annotation { "Feature Type Name" : "Feature", "Feature Type Description" : "" }
export const myFeature = defineFeature(function(context is Context, id is Id, definition is map)
    precondition{}
    {
        {
            var Q0;
            Q0=qCreatedBy(makeId("Top.planeOp"),FACE);
            var sketch = newSketch(context, id + "F0", { "sketchPlane" : qUnion([Q0])});
            skArc(sketch, "E0", {"start": v(-40.95, 7.5) * mm, "mid": v(-48.45, 0) * mm, "end": v(-40.95, -7.5) * mm});
            skArc(sketch, "E1", {"start": v(-40.95, 11.5) * mm, "mid": v(-52.45, 0) * mm, "end": v(-40.95, -11.5) * mm});
            skLineSegment(sketch, "E2", {"start": v(-40.95, 7.5) * mm, "end": v(69.05, 7.5) * mm});
            skLineSegment(sketch, "E3", {"start": v(69.05, 11.5) * mm, "end": v(-40.95, 11.5) * mm});
            skLineSegment(sketch, "E4", {"start": v(-40.95, -7.5) * mm, "end": v(-26.45, -7.5) * mm});
            skLineSegment(sketch, "E5", {"start": v(69.05, -11.5) * mm, "end": v(0, -11.5) * mm});
            skArc(sketch, "E6", {"start": v(-3.98, -7.14) * mm, "mid": v(-13.37, 0.07) * mm, "end": v(-15.85, -11.5) * mm});
            skArc(sketch, "E7", {"start": v(0.66, -4.5) * mm, "mid": v(-10.95, 4.5) * mm, "end": v(-22.57, -4.5) * mm});
            skLineSegment(sketch, "E8.trimOffspring", {"start": v(-15.85, -11.5) * mm, "end": v(-40.95, -11.5) * mm});
            skLineSegment(sketch, "E9.trimOffspring", {"start": v(4.54, -7.5) * mm, "end": v(69.05, -7.5) * mm});
            skPoint(sketch, "E10.visualSharp", {"position": v(1.05, -7.5) * mm});
            skArc(sketch, "E10.filletArc", {"start": v(0.66, -4.5) * mm, "mid": v(2.09, -6.66) * mm, "end": v(4.54, -7.5) * mm});
            skPoint(sketch, "E11.visualSharp", {"position": v(-6.06, -11.5) * mm});
            skArc(sketch, "E11.filletArc", {"start": v(-3.98, -7.14) * mm, "mid": v(-2.95, -10.2) * mm, "end": v(0, -11.5) * mm});
            skPoint(sketch, "E12.visualSharp", {"position": v(-22.95, -7.5) * mm});
            skArc(sketch, "E12.filletArc", {"start": v(-26.45, -7.5) * mm, "mid": v(-24, -6.66) * mm, "end": v(-22.57, -4.5) * mm});
            skLineSegment(sketch, "E13", {"start": v(69.05, 46.2) * mm, "end": v(69.05, -31.55) * mm, "construction": true});
            skLineSegment(sketch, "E14", {"start": v(84.05, 46.35) * mm, "end": v(84.05, -33.76) * mm, "construction": true});
            skLineSegment(sketch, "E15", {"start": v(69.05, 7.5) * mm, "end": v(84.05, 6.19) * mm});
            skLineSegment(sketch, "E16", {"start": v(69.05, -7.5) * mm, "end": v(84.05, -6.19) * mm});
            skLineSegment(sketch, "E17", {"start": v(84.05, -6.19) * mm, "end": v(69.05, -11.5) * mm});
            skLineSegment(sketch, "E18", {"start": v(84.05, 6.19) * mm, "end": v(69.05, 11.5) * mm});
            skLineSegment(sketch, "E19", {"start": v(-15.85, -11.5) * mm, "end": v(0, -11.5) * mm, "construction": true});
            skLineSegment(sketch, "E20", {"start": v(-10.95, 25.74) * mm, "end": v(-10.95, -28.58) * mm, "construction": true});
            skSolve(sketch);
        }
        {
            var Q0;
            Q0=makeQuery(id+"F0.imprint","IMPRINT",FACE,{"disambiguationData":[TD([[makeQuery(id+"F0.imprint","IMPRINT",EDGE,{"derivedFrom":sQuery(id+"F0.wireOp",EDGE,"E0")}),-1.0]])]});
            var Q1;
            {var subQ5=sQuery(id+"F0.wireOp",EDGE,"zYFOjHQd-zfKD-8OcH-rvdT-M6pXXP429t8t.bottom");Q1=makeQuery(id+"F0.imprint","IMPRINT",FACE,{"disambiguationData":[TD([[makeQuery(id+"F0.imprint","IMPRINT",EDGE,{"derivedFrom":subQ5}),-1.0]])]});}
            var Q2;
            {var subQ0=sQuery(id+"F0.wireOp",EDGE,"zYFOjHQd-zfKD-8OcH-rvdT-M6pXXP429t8t.right");var subQ1=sQuery(id+"F0.wireOp",EDGE,"E2");var subQ2=makeQuery(id+"F0.imprint","INTERSECT",VERTEX,{"derivedFrom":[subQ1,subQ0]});Q2=makeQuery(id+"F0.imprint","IMPRINT",FACE,{"disambiguationData":[TD([[makeQuery(id+"F0.imprint","IMPRINT",EDGE,{"disambiguationData":[TD([[subQ2,1.0]])],"derivedFrom":subQ1}),-1.0]])]});}
            var Q3;
            {var subQ5=sQuery(id+"F0.wireOp",EDGE,"zYFOjHQd-zfKD-8OcH-rvdT-M6pXXP429t8t.top");Q3=makeQuery(id+"F0.imprint","IMPRINT",FACE,{"disambiguationData":[TD([[makeQuery(id+"F0.imprint","IMPRINT",EDGE,{"derivedFrom":subQ5}),1.0]])]});}
            extrude(context, id + "F1", {"entities" : qUnion([Q0, Q1, Q2, Q3]), "depth" : 15 * mm, "offsetDistance" : 25 * mm, "symmetric" : true});
        }
        {
            var Q0;
            Q0=qCreatedBy(makeId("Top.planeOp"),FACE);
            var sketch = newSketch(context, id + "F2", { "sketchPlane" : qUnion([Q0])});
            skArc(sketch, "E21.0.0", {"start": v(-15.85, -11.5) * mm, "mid": v(-13.37, 0.07) * mm, "end": v(-3.98, -7.14) * mm, "construction": true});
            skArc(sketch, "E21.0.1", {"start": v(-3.98, -7.14) * mm, "mid": v(-2.95, -10.2) * mm, "end": v(0, -11.5) * mm, "construction": true});
            skLineSegment(sketch, "E21.0.2", {"start": v(0, -11.5) * mm, "end": v(69.05, -11.5) * mm, "construction": true});
            skLineSegment(sketch, "E21.0.3", {"start": v(69.05, -11.5) * mm, "end": v(84.05, -6.19) * mm, "construction": true});
            skLineSegment(sketch, "E21.0.4", {"start": v(84.05, -6.19) * mm, "end": v(69.05, -7.5) * mm, "construction": true});
            skLineSegment(sketch, "E21.0.5", {"start": v(69.05, -7.5) * mm, "end": v(4.54, -7.5) * mm, "construction": true});
            skArc(sketch, "E21.0.6", {"start": v(4.54, -7.5) * mm, "mid": v(2.09, -6.66) * mm, "end": v(0.66, -4.5) * mm, "construction": true});
            skArc(sketch, "E21.0.7", {"start": v(0.66, -4.5) * mm, "mid": v(-10.95, 4.5) * mm, "end": v(-22.57, -4.5) * mm, "construction": true});
            skArc(sketch, "E21.0.8", {"start": v(-22.57, -4.5) * mm, "mid": v(-24, -6.66) * mm, "end": v(-26.45, -7.5) * mm, "construction": true});
            skLineSegment(sketch, "E21.0.9", {"start": v(-26.45, -7.5) * mm, "end": v(-40.95, -7.5) * mm, "construction": true});
            skArc(sketch, "E21.0.10", {"start": v(-40.95, -7.5) * mm, "mid": v(-48.45, 0) * mm, "end": v(-40.95, 7.5) * mm, "construction": true});
            skLineSegment(sketch, "E21.0.11", {"start": v(-40.95, 7.5) * mm, "end": v(69.05, 7.5) * mm, "construction": true});
            skLineSegment(sketch, "E21.0.12", {"start": v(69.05, 7.5) * mm, "end": v(84.05, 6.19) * mm, "construction": true});
            skLineSegment(sketch, "E21.0.13", {"start": v(84.05, 6.19) * mm, "end": v(69.05, 11.5) * mm, "construction": true});
            skLineSegment(sketch, "E21.0.14", {"start": v(69.05, 11.5) * mm, "end": v(-40.95, 11.5) * mm, "construction": true});
            skArc(sketch, "E21.0.15", {"start": v(-40.95, 11.5) * mm, "mid": v(-52.45, 0) * mm, "end": v(-40.95, -11.5) * mm, "construction": true});
            skLineSegment(sketch, "E21.0.16", {"start": v(-40.95, -11.5) * mm, "end": v(-15.85, -11.5) * mm, "construction": true});
            skCircle(sketch, "E22", {"center": v(-40.95, 0) * mm, "radius": 9 * mm});
            skCircle(sketch, "E23", {"center": v(-40.95, 0) * mm, "radius": 10 * mm});
            skLineSegment(sketch, "E24", {"start": v(-17.95, 16.7) * mm, "end": v(-17.95, -20.86) * mm, "construction": true});
            skLineSegment(sketch, "E25", {"start": v(-3.95, 17.93) * mm, "end": v(-3.95, -22.51) * mm, "construction": true});
            skArc(sketch, "E26", {"start": v(-3.95, 7.5) * mm, "mid": v(-6.58, 4.87) * mm, "end": v(-3.95, 2.25) * mm});
            skArc(sketch, "E27", {"start": v(-17.95, 2.25) * mm, "mid": v(-15.33, 4.87) * mm, "end": v(-17.95, 7.5) * mm});
            skLineSegment(sketch, "E28", {"start": v(-17.95, 2.25) * mm, "end": v(-3.95, 2.25) * mm});
            skLineSegment(sketch, "E29", {"start": v(-3.95, 7.5) * mm, "end": v(-17.95, 7.5) * mm});
            skSolve(sketch);
        }
        {
            var Q0;
            Q0=makeQuery(id+"F2.imprint","IMPRINT",FACE,{"disambiguationData":[TD([[makeQuery(id+"F2.imprint","IMPRINT",EDGE,{"derivedFrom":sQuery(id+"F2.wireOp",EDGE,"E26")}),-1.0]])]});
            extrude(context, id + "F3", {"entities" : qUnion([Q0]), "operationType" : NewBodyOperationType.ADD, "depth" : 15 * mm, "offsetDistance" : 25 * mm, "symmetric" : true});
        }
        {
            var Q0;
            Q0=makeQuery(id+"F3.boolean.opBoolean","MERGE",FACE,{"derivedFrom":[makeQuery(id+"F1.opExtrude","CAP_FACE",FACE,{"disambiguationData":[OSD([sQuery(id+"F0.wireOp",EDGE,"E0"),sQuery(id+"F0.wireOp",EDGE,"E1"),sQuery(id+"F0.wireOp",EDGE,"E2"),sQuery(id+"F0.wireOp",EDGE,"E3"),sQuery(id+"F0.wireOp",EDGE,"E4"),sQuery(id+"F0.wireOp",EDGE,"E5"),sQuery(id+"F0.wireOp",EDGE,"E6"),sQuery(id+"F0.wireOp",EDGE,"E7"),sQuery(id+"F0.wireOp",EDGE,"E8.trimOffspring"),sQuery(id+"F0.wireOp",EDGE,"E9.trimOffspring"),sQuery(id+"F0.wireOp",EDGE,"E10.filletArc"),sQuery(id+"F0.wireOp",EDGE,"E11.filletArc"),sQuery(id+"F0.wireOp",EDGE,"E12.filletArc"),sQuery(id+"F0.wireOp",EDGE,"E15"),sQuery(id+"F0.wireOp",EDGE,"E16"),sQuery(id+"F0.wireOp",EDGE,"E17"),sQuery(id+"F0.wireOp",EDGE,"E18")])],"isStart":false}),makeQuery(id+"F3.opExtrude","CAP_FACE",FACE,{"disambiguationData":[OSD([sQuery(id+"F2.wireOp",EDGE,"E22"),sQuery(id+"F2.wireOp",EDGE,"E23")])],"isStart":false})]});
            var sketch = newSketch(context, id + "F4", { "sketchPlane" : qUnion([Q0])});
            skCircle(sketch, "E30", {"center": v(71.04, 7.33) * mm, "radius": 0.75 * mm});
            skCircle(sketch, "E31", {"center": v(73.03, -7.15) * mm, "radius": 0.75 * mm});
            skCircle(sketch, "E32", {"center": v(77.02, -6.8) * mm, "radius": 0.75 * mm});
            skCircle(sketch, "E33", {"center": v(81, -6.45) * mm, "radius": 0.75 * mm});
            skCircle(sketch, "E34", {"center": v(75.04, 6.98) * mm, "radius": 0.75 * mm});
            skCircle(sketch, "E35", {"center": v(79.04, 6.63) * mm, "radius": 0.75 * mm});
            skSolve(sketch);
        }
        {
            var Q0;
            Q0=makeQuery(id+"F1.opExtrude","SWEPT_EDGE",EDGE,{"disambiguationData":[OSD([sQuery(id+"F0.wireOp",EDGE,"E5"),sQuery(id+"F0.wireOp",EDGE,"E17")])]});
            var Q1;
            Q1=makeQuery(id+"F1.opExtrude","SWEPT_EDGE",EDGE,{"disambiguationData":[OSD([sQuery(id+"F0.wireOp",EDGE,"E3"),sQuery(id+"F0.wireOp",EDGE,"E18")])]});
            var Q2;
            Q2=makeQuery(id+"F1.opExtrude","SWEPT_EDGE",EDGE,{"disambiguationData":[OSD([sQuery(id+"F0.wireOp",EDGE,"E9.trimOffspring"),sQuery(id+"F0.wireOp",EDGE,"E16")])]});
            var Q3;
            Q3=makeQuery(id+"F1.opExtrude","SWEPT_EDGE",EDGE,{"disambiguationData":[OSD([sQuery(id+"F0.wireOp",EDGE,"E2"),sQuery(id+"F0.wireOp",EDGE,"E15")])]});
            fillet(context, id + "F5", {"entities" : qUnion([Q0, Q1, Q2, Q3]), "radius" : 30 * mm, "tangentPropagation" : true, "allowEdgeOverflow" : false});
        }
        {
            var Q0;
            Q0=makeQuery(id+"F1.opExtrude","SWEPT_FACE",FACE,{"disambiguationData":[OSD([sQuery(id+"F0.wireOp",EDGE,"E3")])]});
            var sketch = newSketch(context, id + "F6", { "sketchPlane" : qUnion([Q0])});
            skText(sketch, "E36", { "text": "Paulo Cabrita\n                            Fotografia estenopeica", "fontName": "OpenSans-Bold.ttf"});
            skLineSegment(sketch, "E37", {"start": v(-63.9, 0) * mm, "end": v(40.95, 0) * mm, "construction": true});
            skPoint(sketch, "E38", {"position": v(-11.47, 0) * mm});
            skLineSegment(sketch, "E39", {"start": v(-63.9, -7.5) * mm, "end": v(-63.9, 7.5) * mm, "construction": true});
            const initialGuessF6  = {"E36": [-0.07596, 0.0025, 1, 0, 0.00385]};
            skSetInitialGuess(sketch, initialGuessF6);
            skSolve(sketch);
        }
        {
            var Q0;
            Q0 = qSketchRegion(id + "F6", true);
            extrude(context, id + "F7", {"entities" : qUnion([Q0]), "operationType" : NewBodyOperationType.REMOVE, "oppositeDirection" : true, "depth" : 1.5 * mm, "offsetDistance" : 25 * mm});
        }
        {
            var Q0;
            Q0=qCreatedBy(makeId("Front.planeOp"),FACE);
            var sketch = newSketch(context, id + "F8", { "sketchPlane" : qUnion([Q0])});
            skText(sketch, "E40", { "text": "Paulo Cabrita\n                            Fotografia estenopeica", "fontName": "OpenSans-Bold.ttf"});
            const initialGuessF8  = {"E40": [-0.0257, 0.05, 1, 0, 0.00385]};
            skSetInitialGuess(sketch, initialGuessF8);
            skSolve(sketch);
        }
        {
            var Q0;
            Q0 = qSketchRegion(id + "F8", true);
            extrude(context, id + "F9", {"entities" : qUnion([Q0]), "depth" : 1.5 * mm, "offsetDistance" : 25 * mm});
        }
    });